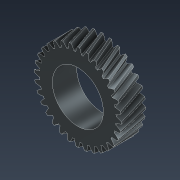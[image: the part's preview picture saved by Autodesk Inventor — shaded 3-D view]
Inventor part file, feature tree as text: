
AUTODESK INVENTOR PART (.ipt)
format: ipt  version: 2022 (Build 260153000, 153)  size: 539,136 bytes
history: native  units: mm (DEFAULTED — no unit token found)
features: plane x3, other x3, sketch x3, extrude x2
ambient origin geometry x8: Origin, YZ Plane, XZ Plane, XY Plane, X Axis, Y Axis, Z Axis, Center Point
bodies: Solid1 (feature_tree)
feature tree (11):
  extrude  "Extrusion1"  Depth=20.0mm TaperAngle=0.0deg
  plane  "Work Plane2"
  plane  "Work Plane8"
  plane  "Work Plane9"
  other  "Spur Gear"
  extrude  "Extrusion2"  Depth=10.0mm TaperAngle=0.0deg
  sketch  "Sketch1"  dims[d0=71.898447mm d1=20.0mm d2=0.0mm]
  sketch  "Sketch2"  dims[d3=68.107377mm d4=10.0mm d5=0.0mm]
  other  "Srf1"
  sketch  "Sketch3"  dims[d16=104.0mm d17=0.0mm d34=0.981748mm d39=0.0mm d41=0.0mm d43=104.0mm d46=104.0mm d47=0.0mm d48=0.0mm d49=42.0mm d50=0.0mm d51=0.0mm]
  other  "Pitch Diameter"
